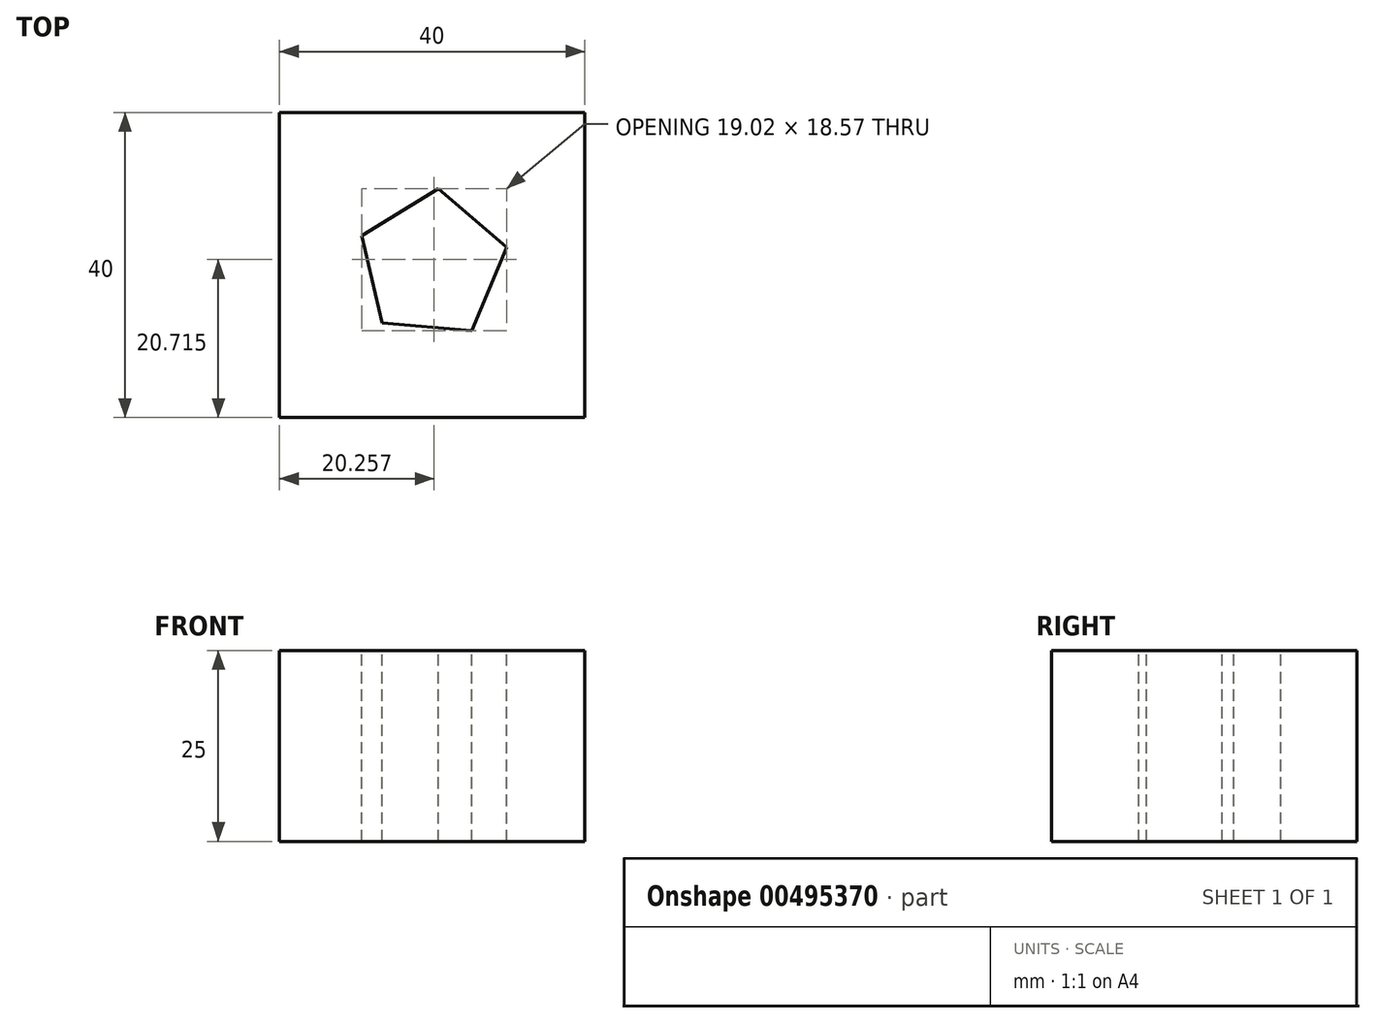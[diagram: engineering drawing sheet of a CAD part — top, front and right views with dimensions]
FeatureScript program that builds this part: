
annotation { "Feature Type Name" : "Feature", "Feature Type Description" : "" }
export const myFeature = defineFeature(function(context is Context, id is Id, definition is map)
    precondition{}
    {
        {
            var Q0;
            Q0=qCreatedBy(makeId("Top.planeOp"),FACE);
            var sketch = newSketch(context, id + "F0", { "sketchPlane" : qUnion([Q0])});
            skLineSegment(sketch, "E0.bottom", {"start": v(-65.04, 15.4) * mm, "end": v(-25.04, 15.4) * mm});
            skLineSegment(sketch, "E0.top", {"start": v(-65.04, -24.6) * mm, "end": v(-25.04, -24.6) * mm});
            skLineSegment(sketch, "E0.left", {"start": v(-65.04, 15.4) * mm, "end": v(-65.04, -24.6) * mm});
            skLineSegment(sketch, "E0.right", {"start": v(-25.04, 15.4) * mm, "end": v(-25.04, -24.6) * mm});
            skSolve(sketch);
        }
        {
            var Q0;
            Q0=makeQuery(id+"F0.imprint","IMPRINT",FACE,{"disambiguationData":[TD([[makeQuery(id+"F0.imprint","IMPRINT",EDGE,{"derivedFrom":sQuery(id+"F0.wireOp",EDGE,"E0.bottom")}),-1.0]])]});
            extrude(context, id + "F1", {"entities" : qUnion([Q0]), "depth" : 25 * mm});
        }
        {
            var Q0;
            Q0=makeQuery(id+"F1.opExtrude","CAP_FACE",FACE,{"disambiguationData":[OSD([sQuery(id+"F0.wireOp",EDGE,"E0.bottom"),sQuery(id+"F0.wireOp",EDGE,"E0.top"),sQuery(id+"F0.wireOp",EDGE,"E0.left"),sQuery(id+"F0.wireOp",EDGE,"E0.right")])],"isStart":false});
            var sketch = newSketch(context, id + "F2", { "sketchPlane" : qUnion([Q0])});
            skCircle(sketch, "E1.cCircle", {"center": v(-45.04, -4.6) * mm, "radius": 10.03 * mm, "construction": true});
            skLineSegment(sketch, "E1.0", {"start": v(-35.27, -2.29) * mm, "end": v(-39.82, -13.17) * mm});
            skLineSegment(sketch, "E1.1", {"start": v(-39.82, -13.17) * mm, "end": v(-51.58, -12.2) * mm});
            skLineSegment(sketch, "E1.2", {"start": v(-51.58, -12.2) * mm, "end": v(-54.3, -0.73) * mm});
            skLineSegment(sketch, "E1.3", {"start": v(-54.3, -0.73) * mm, "end": v(-44.22, 5.4) * mm});
            skLineSegment(sketch, "E1.4", {"start": v(-44.22, 5.4) * mm, "end": v(-35.27, -2.29) * mm});
            skSolve(sketch);
        }
        {
            var Q0;
            Q0=makeQuery(id+"F2.imprint","IMPRINT",FACE,{"disambiguationData":[TD([[makeQuery(id+"F2.imprint","IMPRINT",EDGE,{"derivedFrom":sQuery(id+"F2.wireOp",EDGE,"E1.0")}),-1.0]])]});
            extrude(context, id + "F3", {"entities" : qUnion([Q0]), "operationType" : NewBodyOperationType.REMOVE, "endBound" : BoundingType.THROUGH_ALL, "oppositeDirection" : true, "depth" : 25 * mm});
        }
    });
